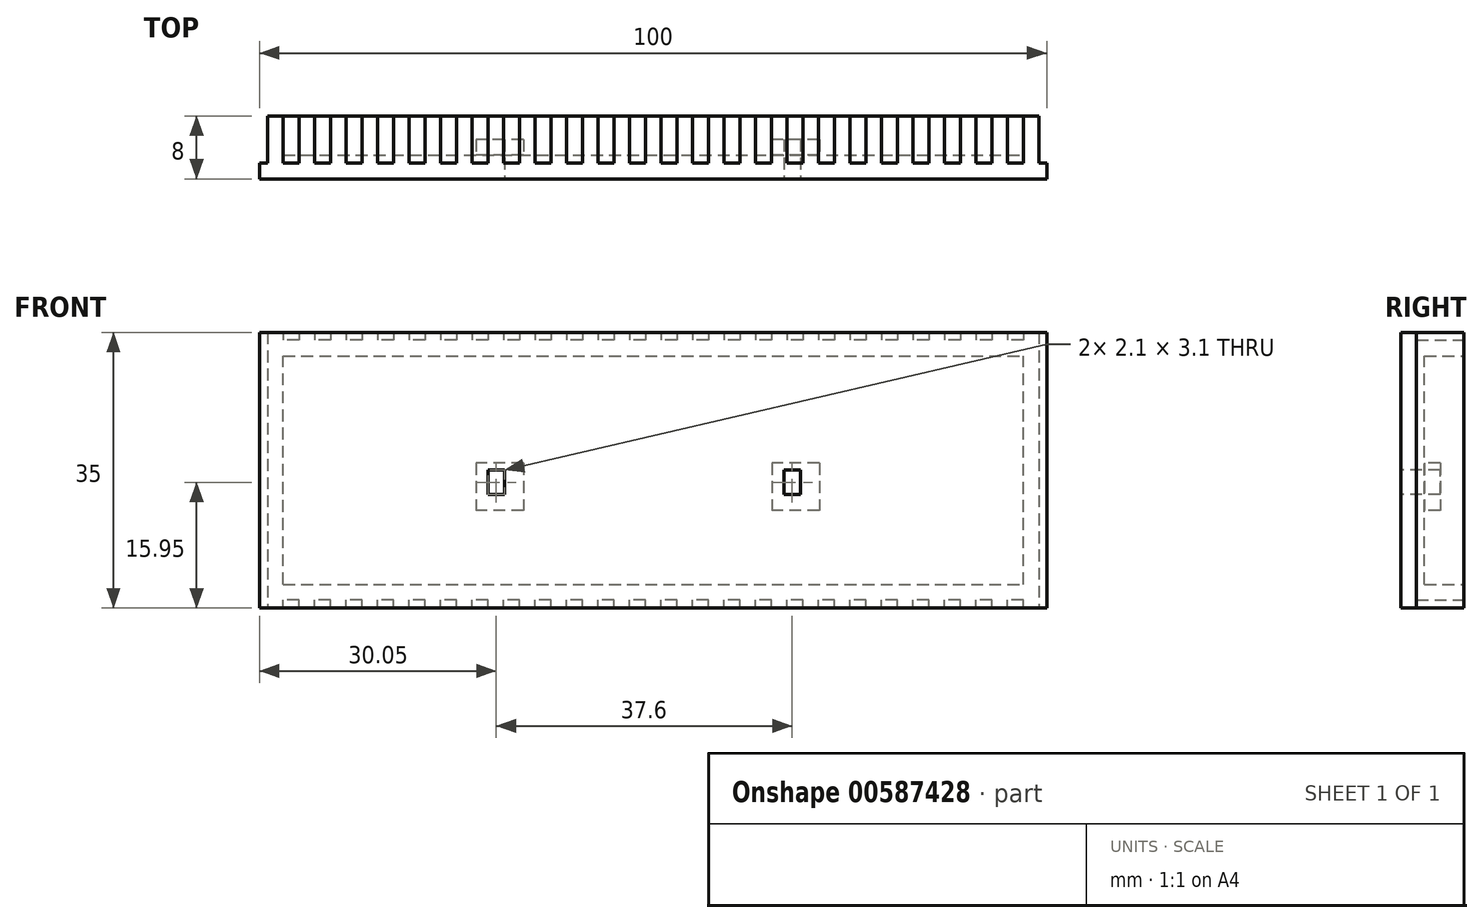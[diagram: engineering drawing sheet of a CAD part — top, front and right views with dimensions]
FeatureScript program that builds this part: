
annotation { "Feature Type Name" : "Feature", "Feature Type Description" : "" }
export const myFeature = defineFeature(function(context is Context, id is Id, definition is map)
    precondition{}
    {
        {
            var Q0;
            Q0=qCreatedBy(makeId("Front.planeOp"),FACE);
            var sketch = newSketch(context, id + "F0", { "sketchPlane" : qUnion([Q0])});
            skLineSegment(sketch, "E0.bottom", {"start": v(0, 0) * mm, "end": v(100, 0) * mm});
            skLineSegment(sketch, "E0.top", {"start": v(0, 35) * mm, "end": v(100, 35) * mm});
            skLineSegment(sketch, "E0.left", {"start": v(0, 0) * mm, "end": v(0, 35) * mm});
            skLineSegment(sketch, "E0.right", {"start": v(100, 0) * mm, "end": v(100, 35) * mm});
            skSolve(sketch);
        }
        {
            var Q0;
            Q0=makeQuery(id+"F0.imprint","IMPRINT",FACE,{"disambiguationData":[TD([[makeQuery(id+"F0.imprint","IMPRINT",EDGE,{"derivedFrom":sQuery(id+"F0.wireOp",EDGE,"E0.bottom")}),1.0]])]});
            extrude(context, id + "F1", {"entities" : qUnion([Q0]), "endBound" : BoundingType.SYMMETRIC, "depth" : 8 * mm, "offsetDistance" : 25 * mm});
        }
        {
            var Q0;
            Q0=makeQuery(id+"F1.opExtrude","CAP_FACE",FACE,{"disambiguationData":[OSD([sQuery(id+"F0.wireOp",EDGE,"E0.bottom"),sQuery(id+"F0.wireOp",EDGE,"E0.top"),sQuery(id+"F0.wireOp",EDGE,"E0.left"),sQuery(id+"F0.wireOp",EDGE,"E0.right")])],"isStart":true});
            shell(context, id + "F2", {"entities" : qUnion([Q0]), "thickness" : 3 * mm});
        }
        {
            var Q0;
            Q0=makeQuery(id+"F1.opExtrude","CAP_FACE",FACE,{"disambiguationData":[OSD([sQuery(id+"F0.wireOp",EDGE,"E0.bottom"),sQuery(id+"F0.wireOp",EDGE,"E0.top"),sQuery(id+"F0.wireOp",EDGE,"E0.left"),sQuery(id+"F0.wireOp",EDGE,"E0.right")])],"isStart":true});
            var sketch = newSketch(context, id + "F3", { "sketchPlane" : qUnion([Q0])});
            skLineSegment(sketch, "E1.bottom", {"start": v(-100, 35) * mm, "end": v(-99, 35) * mm});
            skLineSegment(sketch, "E1.top", {"start": v(-100, 0) * mm, "end": v(-99, 0) * mm});
            skLineSegment(sketch, "E1.left", {"start": v(-100, 35) * mm, "end": v(-100, 0) * mm});
            skLineSegment(sketch, "E1.right", {"start": v(-99, 35) * mm, "end": v(-99, 0) * mm});
            skLineSegment(sketch, "E2.bottom", {"start": v(0, 35) * mm, "end": v(-1, 35) * mm});
            skLineSegment(sketch, "E2.top", {"start": v(0, 0) * mm, "end": v(-1, 0) * mm});
            skLineSegment(sketch, "E2.left", {"start": v(0, 35) * mm, "end": v(0, 0) * mm});
            skLineSegment(sketch, "E2.right", {"start": v(-1, 35) * mm, "end": v(-1, 0) * mm});
            skSolve(sketch);
        }
        {
            var Q0;
            Q0 = qSketchRegion(id + "F3", true);
            extrude(context, id + "F4", {"entities" : qUnion([Q0]), "operationType" : NewBodyOperationType.REMOVE, "oppositeDirection" : true, "depth" : 6 * mm, "offsetDistance" : 25 * mm});
        }
        {
            var Q0;
            Q0=makeQuery(id+"F1.opExtrude","CAP_FACE",FACE,{"disambiguationData":[OSD([sQuery(id+"F0.wireOp",EDGE,"E0.bottom"),sQuery(id+"F0.wireOp",EDGE,"E0.top"),sQuery(id+"F0.wireOp",EDGE,"E0.left"),sQuery(id+"F0.wireOp",EDGE,"E0.right")])],"isStart":true});
            var sketch = newSketch(context, id + "F5", { "sketchPlane" : qUnion([Q0])});
            skLineSegment(sketch, "E3.bottom", {"start": v(-97, 35) * mm, "end": v(-95, 35) * mm});
            skLineSegment(sketch, "E3.top", {"start": v(-97, 34) * mm, "end": v(-95, 34) * mm});
            skLineSegment(sketch, "E3.left", {"start": v(-97, 35) * mm, "end": v(-97, 34) * mm});
            skLineSegment(sketch, "E3.right", {"start": v(-95, 35) * mm, "end": v(-95, 34) * mm});
            skLineSegment(sketch, "E4.bottom", {"start": v(-97, 0) * mm, "end": v(-95, 0) * mm});
            skLineSegment(sketch, "E4.top", {"start": v(-97, 1) * mm, "end": v(-95, 1) * mm});
            skLineSegment(sketch, "E4.left", {"start": v(-97, 0) * mm, "end": v(-97, 1) * mm});
            skLineSegment(sketch, "E4.right", {"start": v(-95, 0) * mm, "end": v(-95, 1) * mm});
            skLineSegment(sketch, "E5.1.0.0", {"start": v(-93, 35) * mm, "end": v(-91, 35) * mm});
            skLineSegment(sketch, "E5.1.0.1", {"start": v(-91, 35) * mm, "end": v(-91, 34) * mm});
            skLineSegment(sketch, "E5.1.0.2", {"start": v(-93, 34) * mm, "end": v(-91, 34) * mm});
            skLineSegment(sketch, "E5.1.0.3", {"start": v(-93, 35) * mm, "end": v(-93, 34) * mm});
            skLineSegment(sketch, "E5.1.0.4", {"start": v(-91, 0) * mm, "end": v(-91, 1) * mm});
            skLineSegment(sketch, "E5.1.0.5", {"start": v(-93, 1) * mm, "end": v(-91, 1) * mm});
            skLineSegment(sketch, "E5.1.0.6", {"start": v(-93, 0) * mm, "end": v(-91, 0) * mm});
            skLineSegment(sketch, "E5.1.0.7", {"start": v(-93, 0) * mm, "end": v(-93, 1) * mm});
            skLineSegment(sketch, "E5.2.0.0", {"start": v(-89, 35) * mm, "end": v(-87, 35) * mm});
            skLineSegment(sketch, "E5.2.0.1", {"start": v(-87, 35) * mm, "end": v(-87, 34) * mm});
            skLineSegment(sketch, "E5.2.0.2", {"start": v(-89, 34) * mm, "end": v(-87, 34) * mm});
            skLineSegment(sketch, "E5.2.0.3", {"start": v(-89, 35) * mm, "end": v(-89, 34) * mm});
            skLineSegment(sketch, "E5.2.0.4", {"start": v(-87, 0) * mm, "end": v(-87, 1) * mm});
            skLineSegment(sketch, "E5.2.0.5", {"start": v(-89, 1) * mm, "end": v(-87, 1) * mm});
            skLineSegment(sketch, "E5.2.0.6", {"start": v(-89, 0) * mm, "end": v(-87, 0) * mm});
            skLineSegment(sketch, "E5.2.0.7", {"start": v(-89, 0) * mm, "end": v(-89, 1) * mm});
            skLineSegment(sketch, "E5.3.0.0", {"start": v(-85, 35) * mm, "end": v(-83, 35) * mm});
            skLineSegment(sketch, "E5.3.0.1", {"start": v(-83, 35) * mm, "end": v(-83, 34) * mm});
            skLineSegment(sketch, "E5.3.0.2", {"start": v(-85, 34) * mm, "end": v(-83, 34) * mm});
            skLineSegment(sketch, "E5.3.0.3", {"start": v(-85, 35) * mm, "end": v(-85, 34) * mm});
            skLineSegment(sketch, "E5.3.0.4", {"start": v(-83, 0) * mm, "end": v(-83, 1) * mm});
            skLineSegment(sketch, "E5.3.0.5", {"start": v(-85, 1) * mm, "end": v(-83, 1) * mm});
            skLineSegment(sketch, "E5.3.0.6", {"start": v(-85, 0) * mm, "end": v(-83, 0) * mm});
            skLineSegment(sketch, "E5.3.0.7", {"start": v(-85, 0) * mm, "end": v(-85, 1) * mm});
            skLineSegment(sketch, "E5.4.0.0", {"start": v(-81, 35) * mm, "end": v(-79, 35) * mm});
            skLineSegment(sketch, "E5.4.0.1", {"start": v(-79, 35) * mm, "end": v(-79, 34) * mm});
            skLineSegment(sketch, "E5.4.0.2", {"start": v(-81, 34) * mm, "end": v(-79, 34) * mm});
            skLineSegment(sketch, "E5.4.0.3", {"start": v(-81, 35) * mm, "end": v(-81, 34) * mm});
            skLineSegment(sketch, "E5.4.0.4", {"start": v(-79, 0) * mm, "end": v(-79, 1) * mm});
            skLineSegment(sketch, "E5.4.0.5", {"start": v(-81, 1) * mm, "end": v(-79, 1) * mm});
            skLineSegment(sketch, "E5.4.0.6", {"start": v(-81, 0) * mm, "end": v(-79, 0) * mm});
            skLineSegment(sketch, "E5.4.0.7", {"start": v(-81, 0) * mm, "end": v(-81, 1) * mm});
            skLineSegment(sketch, "E5.5.0.0", {"start": v(-77, 35) * mm, "end": v(-75, 35) * mm});
            skLineSegment(sketch, "E5.5.0.1", {"start": v(-75, 35) * mm, "end": v(-75, 34) * mm});
            skLineSegment(sketch, "E5.5.0.2", {"start": v(-77, 34) * mm, "end": v(-75, 34) * mm});
            skLineSegment(sketch, "E5.5.0.3", {"start": v(-77, 35) * mm, "end": v(-77, 34) * mm});
            skLineSegment(sketch, "E5.5.0.4", {"start": v(-75, 0) * mm, "end": v(-75, 1) * mm});
            skLineSegment(sketch, "E5.5.0.5", {"start": v(-77, 1) * mm, "end": v(-75, 1) * mm});
            skLineSegment(sketch, "E5.5.0.6", {"start": v(-77, 0) * mm, "end": v(-75, 0) * mm});
            skLineSegment(sketch, "E5.5.0.7", {"start": v(-77, 0) * mm, "end": v(-77, 1) * mm});
            skLineSegment(sketch, "E5.6.0.0", {"start": v(-73, 35) * mm, "end": v(-71, 35) * mm});
            skLineSegment(sketch, "E5.6.0.1", {"start": v(-71, 35) * mm, "end": v(-71, 34) * mm});
            skLineSegment(sketch, "E5.6.0.2", {"start": v(-73, 34) * mm, "end": v(-71, 34) * mm});
            skLineSegment(sketch, "E5.6.0.3", {"start": v(-73, 35) * mm, "end": v(-73, 34) * mm});
            skLineSegment(sketch, "E5.6.0.4", {"start": v(-71, 0) * mm, "end": v(-71, 1) * mm});
            skLineSegment(sketch, "E5.6.0.5", {"start": v(-73, 1) * mm, "end": v(-71, 1) * mm});
            skLineSegment(sketch, "E5.6.0.6", {"start": v(-73, 0) * mm, "end": v(-71, 0) * mm});
            skLineSegment(sketch, "E5.6.0.7", {"start": v(-73, 0) * mm, "end": v(-73, 1) * mm});
            skLineSegment(sketch, "E5.7.0.0", {"start": v(-69, 35) * mm, "end": v(-67, 35) * mm});
            skLineSegment(sketch, "E5.7.0.1", {"start": v(-67, 35) * mm, "end": v(-67, 34) * mm});
            skLineSegment(sketch, "E5.7.0.2", {"start": v(-69, 34) * mm, "end": v(-67, 34) * mm});
            skLineSegment(sketch, "E5.7.0.3", {"start": v(-69, 35) * mm, "end": v(-69, 34) * mm});
            skLineSegment(sketch, "E5.7.0.4", {"start": v(-67, 0) * mm, "end": v(-67, 1) * mm});
            skLineSegment(sketch, "E5.7.0.5", {"start": v(-69, 1) * mm, "end": v(-67, 1) * mm});
            skLineSegment(sketch, "E5.7.0.6", {"start": v(-69, 0) * mm, "end": v(-67, 0) * mm});
            skLineSegment(sketch, "E5.7.0.7", {"start": v(-69, 0) * mm, "end": v(-69, 1) * mm});
            skLineSegment(sketch, "E5.8.0.0", {"start": v(-65, 35) * mm, "end": v(-63, 35) * mm});
            skLineSegment(sketch, "E5.8.0.1", {"start": v(-63, 35) * mm, "end": v(-63, 34) * mm});
            skLineSegment(sketch, "E5.8.0.2", {"start": v(-65, 34) * mm, "end": v(-63, 34) * mm});
            skLineSegment(sketch, "E5.8.0.3", {"start": v(-65, 35) * mm, "end": v(-65, 34) * mm});
            skLineSegment(sketch, "E5.8.0.4", {"start": v(-63, 0) * mm, "end": v(-63, 1) * mm});
            skLineSegment(sketch, "E5.8.0.5", {"start": v(-65, 1) * mm, "end": v(-63, 1) * mm});
            skLineSegment(sketch, "E5.8.0.6", {"start": v(-65, 0) * mm, "end": v(-63, 0) * mm});
            skLineSegment(sketch, "E5.8.0.7", {"start": v(-65, 0) * mm, "end": v(-65, 1) * mm});
            skLineSegment(sketch, "E5.9.0.0", {"start": v(-61, 35) * mm, "end": v(-59, 35) * mm});
            skLineSegment(sketch, "E5.9.0.1", {"start": v(-59, 35) * mm, "end": v(-59, 34) * mm});
            skLineSegment(sketch, "E5.9.0.2", {"start": v(-61, 34) * mm, "end": v(-59, 34) * mm});
            skLineSegment(sketch, "E5.9.0.3", {"start": v(-61, 35) * mm, "end": v(-61, 34) * mm});
            skLineSegment(sketch, "E5.9.0.4", {"start": v(-59, 0) * mm, "end": v(-59, 1) * mm});
            skLineSegment(sketch, "E5.9.0.5", {"start": v(-61, 1) * mm, "end": v(-59, 1) * mm});
            skLineSegment(sketch, "E5.9.0.6", {"start": v(-61, 0) * mm, "end": v(-59, 0) * mm});
            skLineSegment(sketch, "E5.9.0.7", {"start": v(-61, 0) * mm, "end": v(-61, 1) * mm});
            skLineSegment(sketch, "E5.10.0.0", {"start": v(-57, 35) * mm, "end": v(-55, 35) * mm});
            skLineSegment(sketch, "E5.10.0.1", {"start": v(-55, 35) * mm, "end": v(-55, 34) * mm});
            skLineSegment(sketch, "E5.10.0.2", {"start": v(-57, 34) * mm, "end": v(-55, 34) * mm});
            skLineSegment(sketch, "E5.10.0.3", {"start": v(-57, 35) * mm, "end": v(-57, 34) * mm});
            skLineSegment(sketch, "E5.10.0.4", {"start": v(-55, 0) * mm, "end": v(-55, 1) * mm});
            skLineSegment(sketch, "E5.10.0.5", {"start": v(-57, 1) * mm, "end": v(-55, 1) * mm});
            skLineSegment(sketch, "E5.10.0.6", {"start": v(-57, 0) * mm, "end": v(-55, 0) * mm});
            skLineSegment(sketch, "E5.10.0.7", {"start": v(-57, 0) * mm, "end": v(-57, 1) * mm});
            skLineSegment(sketch, "E5.11.0.0", {"start": v(-53, 35) * mm, "end": v(-51, 35) * mm});
            skLineSegment(sketch, "E5.11.0.1", {"start": v(-51, 35) * mm, "end": v(-51, 34) * mm});
            skLineSegment(sketch, "E5.11.0.2", {"start": v(-53, 34) * mm, "end": v(-51, 34) * mm});
            skLineSegment(sketch, "E5.11.0.3", {"start": v(-53, 35) * mm, "end": v(-53, 34) * mm});
            skLineSegment(sketch, "E5.11.0.4", {"start": v(-51, 0) * mm, "end": v(-51, 1) * mm});
            skLineSegment(sketch, "E5.11.0.5", {"start": v(-53, 1) * mm, "end": v(-51, 1) * mm});
            skLineSegment(sketch, "E5.11.0.6", {"start": v(-53, 0) * mm, "end": v(-51, 0) * mm});
            skLineSegment(sketch, "E5.11.0.7", {"start": v(-53, 0) * mm, "end": v(-53, 1) * mm});
            skLineSegment(sketch, "E5.12.0.0", {"start": v(-49, 35) * mm, "end": v(-47, 35) * mm});
            skLineSegment(sketch, "E5.12.0.1", {"start": v(-47, 35) * mm, "end": v(-47, 34) * mm});
            skLineSegment(sketch, "E5.12.0.2", {"start": v(-49, 34) * mm, "end": v(-47, 34) * mm});
            skLineSegment(sketch, "E5.12.0.3", {"start": v(-49, 35) * mm, "end": v(-49, 34) * mm});
            skLineSegment(sketch, "E5.12.0.4", {"start": v(-47, 0) * mm, "end": v(-47, 1) * mm});
            skLineSegment(sketch, "E5.12.0.5", {"start": v(-49, 1) * mm, "end": v(-47, 1) * mm});
            skLineSegment(sketch, "E5.12.0.6", {"start": v(-49, 0) * mm, "end": v(-47, 0) * mm});
            skLineSegment(sketch, "E5.12.0.7", {"start": v(-49, 0) * mm, "end": v(-49, 1) * mm});
            skLineSegment(sketch, "E5.13.0.0", {"start": v(-45, 35) * mm, "end": v(-43, 35) * mm});
            skLineSegment(sketch, "E5.13.0.1", {"start": v(-43, 35) * mm, "end": v(-43, 34) * mm});
            skLineSegment(sketch, "E5.13.0.2", {"start": v(-45, 34) * mm, "end": v(-43, 34) * mm});
            skLineSegment(sketch, "E5.13.0.3", {"start": v(-45, 35) * mm, "end": v(-45, 34) * mm});
            skLineSegment(sketch, "E5.13.0.4", {"start": v(-43, 0) * mm, "end": v(-43, 1) * mm});
            skLineSegment(sketch, "E5.13.0.5", {"start": v(-45, 1) * mm, "end": v(-43, 1) * mm});
            skLineSegment(sketch, "E5.13.0.6", {"start": v(-45, 0) * mm, "end": v(-43, 0) * mm});
            skLineSegment(sketch, "E5.13.0.7", {"start": v(-45, 0) * mm, "end": v(-45, 1) * mm});
            skLineSegment(sketch, "E5.14.0.0", {"start": v(-41, 35) * mm, "end": v(-39, 35) * mm});
            skLineSegment(sketch, "E5.14.0.1", {"start": v(-39, 35) * mm, "end": v(-39, 34) * mm});
            skLineSegment(sketch, "E5.14.0.2", {"start": v(-41, 34) * mm, "end": v(-39, 34) * mm});
            skLineSegment(sketch, "E5.14.0.3", {"start": v(-41, 35) * mm, "end": v(-41, 34) * mm});
            skLineSegment(sketch, "E5.14.0.4", {"start": v(-39, 0) * mm, "end": v(-39, 1) * mm});
            skLineSegment(sketch, "E5.14.0.5", {"start": v(-41, 1) * mm, "end": v(-39, 1) * mm});
            skLineSegment(sketch, "E5.14.0.6", {"start": v(-41, 0) * mm, "end": v(-39, 0) * mm});
            skLineSegment(sketch, "E5.14.0.7", {"start": v(-41, 0) * mm, "end": v(-41, 1) * mm});
            skLineSegment(sketch, "E5.15.0.0", {"start": v(-37, 35) * mm, "end": v(-35, 35) * mm});
            skLineSegment(sketch, "E5.15.0.1", {"start": v(-35, 35) * mm, "end": v(-35, 34) * mm});
            skLineSegment(sketch, "E5.15.0.2", {"start": v(-37, 34) * mm, "end": v(-35, 34) * mm});
            skLineSegment(sketch, "E5.15.0.3", {"start": v(-37, 35) * mm, "end": v(-37, 34) * mm});
            skLineSegment(sketch, "E5.15.0.4", {"start": v(-35, 0) * mm, "end": v(-35, 1) * mm});
            skLineSegment(sketch, "E5.15.0.5", {"start": v(-37, 1) * mm, "end": v(-35, 1) * mm});
            skLineSegment(sketch, "E5.15.0.6", {"start": v(-37, 0) * mm, "end": v(-35, 0) * mm});
            skLineSegment(sketch, "E5.15.0.7", {"start": v(-37, 0) * mm, "end": v(-37, 1) * mm});
            skLineSegment(sketch, "E5.16.0.0", {"start": v(-33, 35) * mm, "end": v(-31, 35) * mm});
            skLineSegment(sketch, "E5.16.0.1", {"start": v(-31, 35) * mm, "end": v(-31, 34) * mm});
            skLineSegment(sketch, "E5.16.0.2", {"start": v(-33, 34) * mm, "end": v(-31, 34) * mm});
            skLineSegment(sketch, "E5.16.0.3", {"start": v(-33, 35) * mm, "end": v(-33, 34) * mm});
            skLineSegment(sketch, "E5.16.0.4", {"start": v(-31, 0) * mm, "end": v(-31, 1) * mm});
            skLineSegment(sketch, "E5.16.0.5", {"start": v(-33, 1) * mm, "end": v(-31, 1) * mm});
            skLineSegment(sketch, "E5.16.0.6", {"start": v(-33, 0) * mm, "end": v(-31, 0) * mm});
            skLineSegment(sketch, "E5.16.0.7", {"start": v(-33, 0) * mm, "end": v(-33, 1) * mm});
            skLineSegment(sketch, "E5.17.0.0", {"start": v(-29, 35) * mm, "end": v(-27, 35) * mm});
            skLineSegment(sketch, "E5.17.0.1", {"start": v(-27, 35) * mm, "end": v(-27, 34) * mm});
            skLineSegment(sketch, "E5.17.0.2", {"start": v(-29, 34) * mm, "end": v(-27, 34) * mm});
            skLineSegment(sketch, "E5.17.0.3", {"start": v(-29, 35) * mm, "end": v(-29, 34) * mm});
            skLineSegment(sketch, "E5.17.0.4", {"start": v(-27, 0) * mm, "end": v(-27, 1) * mm});
            skLineSegment(sketch, "E5.17.0.5", {"start": v(-29, 1) * mm, "end": v(-27, 1) * mm});
            skLineSegment(sketch, "E5.17.0.6", {"start": v(-29, 0) * mm, "end": v(-27, 0) * mm});
            skLineSegment(sketch, "E5.17.0.7", {"start": v(-29, 0) * mm, "end": v(-29, 1) * mm});
            skLineSegment(sketch, "E5.18.0.0", {"start": v(-25, 35) * mm, "end": v(-23, 35) * mm});
            skLineSegment(sketch, "E5.18.0.1", {"start": v(-23, 35) * mm, "end": v(-23, 34) * mm});
            skLineSegment(sketch, "E5.18.0.2", {"start": v(-25, 34) * mm, "end": v(-23, 34) * mm});
            skLineSegment(sketch, "E5.18.0.3", {"start": v(-25, 35) * mm, "end": v(-25, 34) * mm});
            skLineSegment(sketch, "E5.18.0.4", {"start": v(-23, 0) * mm, "end": v(-23, 1) * mm});
            skLineSegment(sketch, "E5.18.0.5", {"start": v(-25, 1) * mm, "end": v(-23, 1) * mm});
            skLineSegment(sketch, "E5.18.0.6", {"start": v(-25, 0) * mm, "end": v(-23, 0) * mm});
            skLineSegment(sketch, "E5.18.0.7", {"start": v(-25, 0) * mm, "end": v(-25, 1) * mm});
            skLineSegment(sketch, "E5.19.0.0", {"start": v(-21, 35) * mm, "end": v(-19, 35) * mm});
            skLineSegment(sketch, "E5.19.0.1", {"start": v(-19, 35) * mm, "end": v(-19, 34) * mm});
            skLineSegment(sketch, "E5.19.0.2", {"start": v(-21, 34) * mm, "end": v(-19, 34) * mm});
            skLineSegment(sketch, "E5.19.0.3", {"start": v(-21, 35) * mm, "end": v(-21, 34) * mm});
            skLineSegment(sketch, "E5.19.0.4", {"start": v(-19, 0) * mm, "end": v(-19, 1) * mm});
            skLineSegment(sketch, "E5.19.0.5", {"start": v(-21, 1) * mm, "end": v(-19, 1) * mm});
            skLineSegment(sketch, "E5.19.0.6", {"start": v(-21, 0) * mm, "end": v(-19, 0) * mm});
            skLineSegment(sketch, "E5.19.0.7", {"start": v(-21, 0) * mm, "end": v(-21, 1) * mm});
            skLineSegment(sketch, "E5.20.0.0", {"start": v(-17, 35) * mm, "end": v(-15, 35) * mm});
            skLineSegment(sketch, "E5.20.0.1", {"start": v(-15, 35) * mm, "end": v(-15, 34) * mm});
            skLineSegment(sketch, "E5.20.0.2", {"start": v(-17, 34) * mm, "end": v(-15, 34) * mm});
            skLineSegment(sketch, "E5.20.0.3", {"start": v(-17, 35) * mm, "end": v(-17, 34) * mm});
            skLineSegment(sketch, "E5.20.0.4", {"start": v(-15, 0) * mm, "end": v(-15, 1) * mm});
            skLineSegment(sketch, "E5.20.0.5", {"start": v(-17, 1) * mm, "end": v(-15, 1) * mm});
            skLineSegment(sketch, "E5.20.0.6", {"start": v(-17, 0) * mm, "end": v(-15, 0) * mm});
            skLineSegment(sketch, "E5.20.0.7", {"start": v(-17, 0) * mm, "end": v(-17, 1) * mm});
            skLineSegment(sketch, "E5.21.0.0", {"start": v(-13, 35) * mm, "end": v(-11, 35) * mm});
            skLineSegment(sketch, "E5.21.0.1", {"start": v(-11, 35) * mm, "end": v(-11, 34) * mm});
            skLineSegment(sketch, "E5.21.0.2", {"start": v(-13, 34) * mm, "end": v(-11, 34) * mm});
            skLineSegment(sketch, "E5.21.0.3", {"start": v(-13, 35) * mm, "end": v(-13, 34) * mm});
            skLineSegment(sketch, "E5.21.0.4", {"start": v(-11, 0) * mm, "end": v(-11, 1) * mm});
            skLineSegment(sketch, "E5.21.0.5", {"start": v(-13, 1) * mm, "end": v(-11, 1) * mm});
            skLineSegment(sketch, "E5.21.0.6", {"start": v(-13, 0) * mm, "end": v(-11, 0) * mm});
            skLineSegment(sketch, "E5.21.0.7", {"start": v(-13, 0) * mm, "end": v(-13, 1) * mm});
            skLineSegment(sketch, "E5.22.0.0", {"start": v(-9, 35) * mm, "end": v(-7, 35) * mm});
            skLineSegment(sketch, "E5.22.0.1", {"start": v(-7, 35) * mm, "end": v(-7, 34) * mm});
            skLineSegment(sketch, "E5.22.0.2", {"start": v(-9, 34) * mm, "end": v(-7, 34) * mm});
            skLineSegment(sketch, "E5.22.0.3", {"start": v(-9, 35) * mm, "end": v(-9, 34) * mm});
            skLineSegment(sketch, "E5.22.0.4", {"start": v(-7, 0) * mm, "end": v(-7, 1) * mm});
            skLineSegment(sketch, "E5.22.0.5", {"start": v(-9, 1) * mm, "end": v(-7, 1) * mm});
            skLineSegment(sketch, "E5.22.0.6", {"start": v(-9, 0) * mm, "end": v(-7, 0) * mm});
            skLineSegment(sketch, "E5.22.0.7", {"start": v(-9, 0) * mm, "end": v(-9, 1) * mm});
            skLineSegment(sketch, "E5.23.0.0", {"start": v(-5, 35) * mm, "end": v(-3, 35) * mm});
            skLineSegment(sketch, "E5.23.0.1", {"start": v(-3, 35) * mm, "end": v(-3, 34) * mm});
            skLineSegment(sketch, "E5.23.0.2", {"start": v(-5, 34) * mm, "end": v(-3, 34) * mm});
            skLineSegment(sketch, "E5.23.0.3", {"start": v(-5, 35) * mm, "end": v(-5, 34) * mm});
            skLineSegment(sketch, "E5.23.0.4", {"start": v(-3, 0) * mm, "end": v(-3, 1) * mm});
            skLineSegment(sketch, "E5.23.0.5", {"start": v(-5, 1) * mm, "end": v(-3, 1) * mm});
            skLineSegment(sketch, "E5.23.0.6", {"start": v(-5, 0) * mm, "end": v(-3, 0) * mm});
            skLineSegment(sketch, "E5.23.0.7", {"start": v(-5, 0) * mm, "end": v(-5, 1) * mm});
            skLineSegment(sketch, "E5.direction1", {"start": v(-97, 35) * mm, "end": v(-93, 35) * mm, "construction": true});
            skSolve(sketch);
        }
        {
            var Q0;
            Q0 = qSketchRegion(id + "F5", true);
            extrude(context, id + "F6", {"entities" : qUnion([Q0]), "operationType" : NewBodyOperationType.REMOVE, "oppositeDirection" : true, "depth" : 6 * mm, "offsetDistance" : 25 * mm});
        }
        {
            var Q0;
            Q0=makeQuery(id+"F1.opExtrude","CAP_FACE",FACE,{"disambiguationData":[OSD([sQuery(id+"F0.wireOp",EDGE,"E0.bottom"),sQuery(id+"F0.wireOp",EDGE,"E0.top"),sQuery(id+"F0.wireOp",EDGE,"E0.left"),sQuery(id+"F0.wireOp",EDGE,"E0.right")])],"isStart":false});
            var sketch = newSketch(context, id + "F7", { "sketchPlane" : qUnion([Q0])});
            skLineSegment(sketch, "E6.bottom", {"start": v(68.7, 14.4) * mm, "end": v(66.6, 14.4) * mm});
            skLineSegment(sketch, "E6.top", {"start": v(68.7, 17.5) * mm, "end": v(66.6, 17.5) * mm});
            skLineSegment(sketch, "E6.left", {"start": v(68.7, 14.4) * mm, "end": v(68.7, 17.5) * mm});
            skLineSegment(sketch, "E6.right", {"start": v(66.6, 14.4) * mm, "end": v(66.6, 17.5) * mm});
            skLineSegment(sketch, "E7.bottom", {"start": v(31.1, 14.4) * mm, "end": v(29, 14.4) * mm});
            skLineSegment(sketch, "E7.top", {"start": v(31.1, 17.5) * mm, "end": v(29, 17.5) * mm});
            skLineSegment(sketch, "E7.left", {"start": v(31.1, 14.4) * mm, "end": v(31.1, 17.5) * mm});
            skLineSegment(sketch, "E7.right", {"start": v(29, 14.4) * mm, "end": v(29, 17.5) * mm});
            skSolve(sketch);
        }
        {
            var Q0;
            Q0 = qSketchRegion(id + "F7", true);
            extrude(context, id + "F8", {"entities" : qUnion([Q0]), "operationType" : NewBodyOperationType.REMOVE, "oppositeDirection" : true, "depth" : 3 * mm, "offsetDistance" : 25 * mm});
        }
        {
            var Q0;
            Q0=makeQuery(id+"F2.opShell","OFFSET_FACE",FACE,{"disambiguationData":[OSD([sQuery(id+"F0.wireOp",EDGE,"E0.bottom"),sQuery(id+"F0.wireOp",EDGE,"E0.top"),sQuery(id+"F0.wireOp",EDGE,"E0.left"),sQuery(id+"F0.wireOp",EDGE,"E0.right")])]});
            var sketch = newSketch(context, id + "F9", { "sketchPlane" : qUnion([Q0])});
            skLineSegment(sketch, "E8.bottom", {"start": v(-71.1, 18.4) * mm, "end": v(-65.1, 18.4) * mm});
            skLineSegment(sketch, "E8.top", {"start": v(-71.1, 12.4) * mm, "end": v(-65.1, 12.4) * mm});
            skLineSegment(sketch, "E8.left", {"start": v(-71.1, 18.4) * mm, "end": v(-71.1, 12.4) * mm});
            skLineSegment(sketch, "E8.right", {"start": v(-65.1, 18.4) * mm, "end": v(-65.1, 12.4) * mm});
            skLineSegment(sketch, "E9.bottom", {"start": v(-33.5, 18.4) * mm, "end": v(-27.5, 18.4) * mm});
            skLineSegment(sketch, "E9.top", {"start": v(-33.5, 12.4) * mm, "end": v(-27.5, 12.4) * mm});
            skLineSegment(sketch, "E9.left", {"start": v(-33.5, 18.4) * mm, "end": v(-33.5, 12.4) * mm});
            skLineSegment(sketch, "E9.right", {"start": v(-27.5, 18.4) * mm, "end": v(-27.5, 12.4) * mm});
            skLineSegment(sketch, "E10.bottom", {"start": v(-66.6, 17.5) * mm, "end": v(-68.7, 17.5) * mm});
            skLineSegment(sketch, "E10.top", {"start": v(-66.6, 14.4) * mm, "end": v(-68.7, 14.4) * mm});
            skLineSegment(sketch, "E10.left", {"start": v(-66.6, 17.5) * mm, "end": v(-66.6, 14.4) * mm});
            skLineSegment(sketch, "E10.right", {"start": v(-68.7, 17.5) * mm, "end": v(-68.7, 14.4) * mm});
            skLineSegment(sketch, "E11.bottom", {"start": v(-29, 17.5) * mm, "end": v(-31.1, 17.5) * mm});
            skLineSegment(sketch, "E11.top", {"start": v(-29, 14.4) * mm, "end": v(-31.1, 14.4) * mm});
            skLineSegment(sketch, "E11.left", {"start": v(-29, 17.5) * mm, "end": v(-29, 14.4) * mm});
            skLineSegment(sketch, "E11.right", {"start": v(-31.1, 17.5) * mm, "end": v(-31.1, 14.4) * mm});
            skSolve(sketch);
        }
        {
            var Q0;
            Q0 = qSketchRegion(id + "F9", true);
            extrude(context, id + "F10", {"entities" : qUnion([Q0]), "operationType" : NewBodyOperationType.ADD, "depth" : 2 * mm, "offsetDistance" : 25 * mm});
        }
    });
